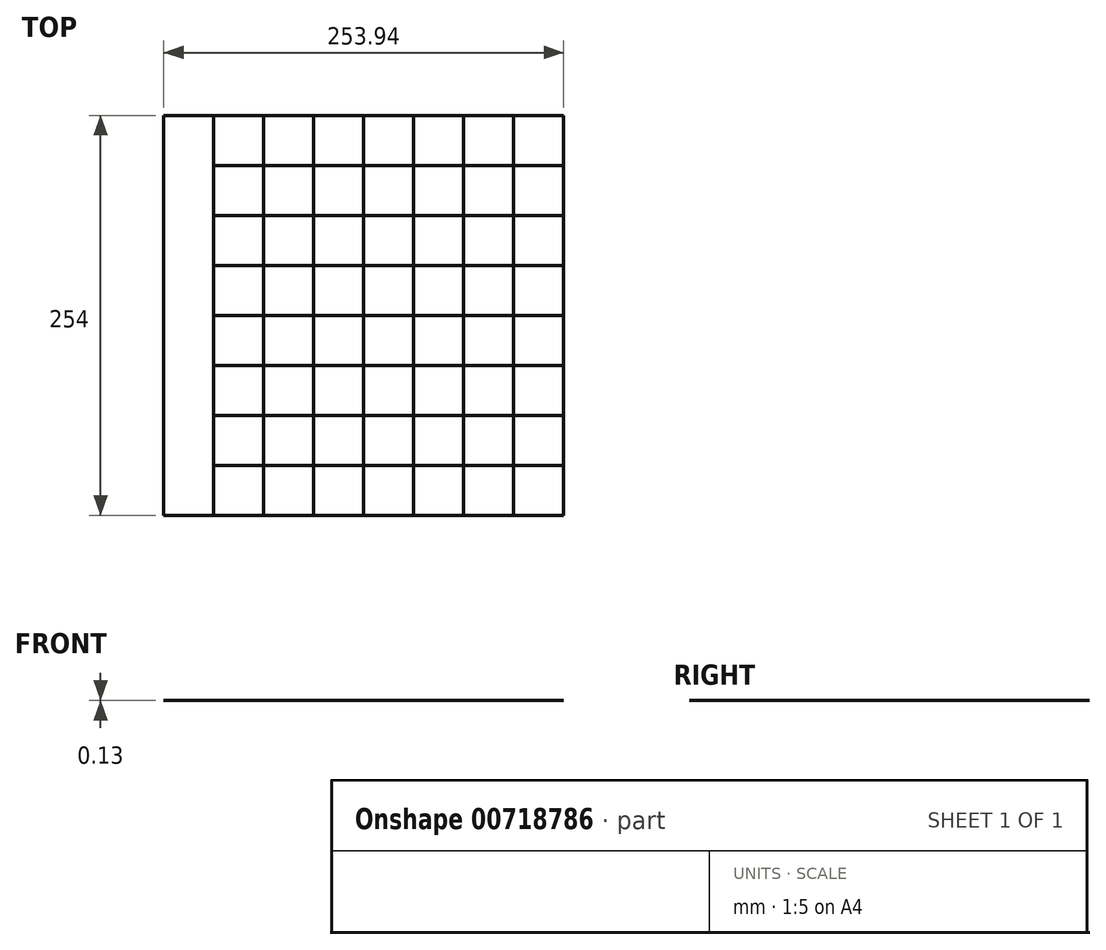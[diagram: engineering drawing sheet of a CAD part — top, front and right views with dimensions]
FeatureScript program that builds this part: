
annotation { "Feature Type Name" : "Feature", "Feature Type Description" : "" }
export const myFeature = defineFeature(function(context is Context, id is Id, definition is map)
    precondition{}
    {
        {
            var Q0;
            Q0=qCreatedBy(makeId("Top.planeOp"),FACE);
            var sketch = newSketch(context, id + "F0", { "sketchPlane" : qUnion([Q0])});
            skLineSegment(sketch, "E0.bottom", {"start": v(-104.6, 172.24) * mm, "end": v(149.4, 172.24) * mm});
            skLineSegment(sketch, "E0.top", {"start": v(-104.6, -81.76) * mm, "end": v(149.4, -81.76) * mm});
            skLineSegment(sketch, "E0.left", {"start": v(-104.6, 172.24) * mm, "end": v(-104.6, -81.76) * mm});
            skLineSegment(sketch, "E0.right", {"start": v(149.4, 172.24) * mm, "end": v(149.4, -81.76) * mm});
            skLineSegment(sketch, "E1", {"start": v(22.4, 172.24) * mm, "end": v(22.4, -81.76) * mm});
            skLineSegment(sketch, "E2", {"start": v(-41.1, 172.24) * mm, "end": v(-41.1, -81.76) * mm});
            skLineSegment(sketch, "E3", {"start": v(-72.86, 172.24) * mm, "end": v(-72.86, -81.76) * mm});
            skLineSegment(sketch, "E4", {"start": v(-9.36, 172.24) * mm, "end": v(-9.36, -81.76) * mm});
            skLineSegment(sketch, "E5", {"start": v(85.9, 172.24) * mm, "end": v(85.9, -81.76) * mm});
            skLineSegment(sketch, "E6", {"start": v(54.14, 172.24) * mm, "end": v(54.14, -81.76) * mm});
            skLineSegment(sketch, "E7", {"start": v(117.64, 172.24) * mm, "end": v(117.64, -81.76) * mm});
            skLineSegment(sketch, "E8.bottom", {"start": v(-104.55, -81.76) * mm, "end": v(-104.55, 172.24) * mm});
            skLineSegment(sketch, "E8.top", {"start": v(-72.8, -81.76) * mm, "end": v(-72.8, 172.24) * mm});
            skLineSegment(sketch, "E8.left", {"start": v(-104.55, -81.76) * mm, "end": v(-72.8, -81.76) * mm});
            skLineSegment(sketch, "E8.right", {"start": v(-104.55, 172.24) * mm, "end": v(-72.8, 172.24) * mm});
            skLineSegment(sketch, "E9", {"start": v(-104.55, 140.5) * mm, "end": v(149.4, 140.5) * mm});
            skLineSegment(sketch, "E10", {"start": v(-104.55, 108.74) * mm, "end": v(149.4, 108.74) * mm});
            skLineSegment(sketch, "E11", {"start": v(-104.55, 77) * mm, "end": v(149.4, 77) * mm});
            skLineSegment(sketch, "E12", {"start": v(-104.55, 45.24) * mm, "end": v(149.4, 45.24) * mm});
            skLineSegment(sketch, "E13", {"start": v(-104.55, 13.5) * mm, "end": v(149.4, 13.5) * mm});
            skLineSegment(sketch, "E14", {"start": v(-104.55, -18.26) * mm, "end": v(149.4, -18.26) * mm});
            skLineSegment(sketch, "E15", {"start": v(-104.55, -50) * mm, "end": v(149.4, -50) * mm});
            skSolve(sketch);
        }
        {
            var Q0;
            {var subQ0=sQuery(id+"F0.wireOp",EDGE,"E8.right");var subQ1=sQuery(id+"F0.wireOp",EDGE,"E3");var subQ2=makeQuery(id+"F0.imprint","INTERSECT",VERTEX,{"derivedFrom":[subQ1,subQ0]});Q0=makeQuery(id+"F0.imprint","IMPRINT",FACE,{"disambiguationData":[TD([[makeQuery(id+"F0.imprint","IMPRINT",EDGE,{"disambiguationData":[TD([[subQ2,-1.0]])],"derivedFrom":subQ1}),-1.0]])]});}
            var Q1;
            {var subQ0=sQuery(id+"F0.wireOp",EDGE,"E9");var subQ1=sQuery(id+"F0.wireOp",EDGE,"E2");var subQ2=makeQuery(id+"F0.imprint","INTERSECT",VERTEX,{"derivedFrom":[subQ1,subQ0]});Q1=makeQuery(id+"F0.imprint","IMPRINT",FACE,{"disambiguationData":[TD([[makeQuery(id+"F0.imprint","IMPRINT",EDGE,{"disambiguationData":[TD([[subQ2,-1.0]])],"derivedFrom":subQ1}),-1.0]])]});}
            var Q2;
            {var subQ0=sQuery(id+"F0.wireOp",EDGE,"E2");var subQ1=sQuery(id+"F0.wireOp",EDGE,"E0.bottom");var subQ2=makeQuery(id+"F0.imprint","INTERSECT",VERTEX,{"derivedFrom":[subQ1,subQ0]});Q2=makeQuery(id+"F0.imprint","IMPRINT",FACE,{"disambiguationData":[TD([[makeQuery(id+"F0.imprint","IMPRINT",EDGE,{"disambiguationData":[TD([[subQ2,-1.0]])],"derivedFrom":subQ1}),-1.0]])]});}
            var Q3;
            {var subQ0=sQuery(id+"F0.wireOp",EDGE,"E9");var subQ1=sQuery(id+"F0.wireOp",EDGE,"E1");var subQ2=makeQuery(id+"F0.imprint","INTERSECT",VERTEX,{"derivedFrom":[subQ1,subQ0]});Q3=makeQuery(id+"F0.imprint","IMPRINT",FACE,{"disambiguationData":[TD([[makeQuery(id+"F0.imprint","IMPRINT",EDGE,{"disambiguationData":[TD([[subQ2,-1.0]])],"derivedFrom":subQ1}),-1.0]])]});}
            var Q4;
            {var subQ0=sQuery(id+"F0.wireOp",EDGE,"E1");var subQ1=sQuery(id+"F0.wireOp",EDGE,"E0.bottom");var subQ2=makeQuery(id+"F0.imprint","INTERSECT",VERTEX,{"derivedFrom":[subQ1,subQ0]});Q4=makeQuery(id+"F0.imprint","IMPRINT",FACE,{"disambiguationData":[TD([[makeQuery(id+"F0.imprint","IMPRINT",EDGE,{"disambiguationData":[TD([[subQ2,-1.0]])],"derivedFrom":subQ1}),-1.0]])]});}
            var Q5;
            {var subQ0=sQuery(id+"F0.wireOp",EDGE,"E9");var subQ1=sQuery(id+"F0.wireOp",EDGE,"E5");var subQ2=makeQuery(id+"F0.imprint","INTERSECT",VERTEX,{"derivedFrom":[subQ1,subQ0]});Q5=makeQuery(id+"F0.imprint","IMPRINT",FACE,{"disambiguationData":[TD([[makeQuery(id+"F0.imprint","IMPRINT",EDGE,{"disambiguationData":[TD([[subQ2,-1.0]])],"derivedFrom":subQ1}),-1.0]])]});}
            var Q6;
            {var subQ0=sQuery(id+"F0.wireOp",EDGE,"E5");var subQ1=sQuery(id+"F0.wireOp",EDGE,"E0.bottom");var subQ2=makeQuery(id+"F0.imprint","INTERSECT",VERTEX,{"derivedFrom":[subQ1,subQ0]});Q6=makeQuery(id+"F0.imprint","IMPRINT",FACE,{"disambiguationData":[TD([[makeQuery(id+"F0.imprint","IMPRINT",EDGE,{"disambiguationData":[TD([[subQ2,-1.0]])],"derivedFrom":subQ1}),-1.0]])]});}
            var Q7;
            {var subQ0=sQuery(id+"F0.wireOp",EDGE,"E9");var subQ1=sQuery(id+"F0.wireOp",EDGE,"E0.right");var subQ2=makeQuery(id+"F0.imprint","INTERSECT",VERTEX,{"derivedFrom":[subQ1,subQ0]});Q7=makeQuery(id+"F0.imprint","IMPRINT",FACE,{"disambiguationData":[TD([[makeQuery(id+"F0.imprint","IMPRINT",EDGE,{"disambiguationData":[TD([[subQ2,-1.0]])],"derivedFrom":subQ1}),-1.0]])]});}
            var Q8;
            {var subQ0=sQuery(id+"F0.wireOp",EDGE,"E10");var subQ1=sQuery(id+"F0.wireOp",EDGE,"E5");var subQ2=makeQuery(id+"F0.imprint","INTERSECT",VERTEX,{"derivedFrom":[subQ1,subQ0]});Q8=makeQuery(id+"F0.imprint","IMPRINT",FACE,{"disambiguationData":[TD([[makeQuery(id+"F0.imprint","IMPRINT",EDGE,{"disambiguationData":[TD([[subQ2,-1.0]])],"derivedFrom":subQ1}),1.0]])]});}
            var Q9;
            {var subQ0=sQuery(id+"F0.wireOp",EDGE,"E11");var subQ1=sQuery(id+"F0.wireOp",EDGE,"E5");var subQ2=makeQuery(id+"F0.imprint","INTERSECT",VERTEX,{"derivedFrom":[subQ1,subQ0]});Q9=makeQuery(id+"F0.imprint","IMPRINT",FACE,{"disambiguationData":[TD([[makeQuery(id+"F0.imprint","IMPRINT",EDGE,{"disambiguationData":[TD([[subQ2,-1.0]])],"derivedFrom":subQ1}),-1.0]])]});}
            var Q10;
            {var subQ0=sQuery(id+"F0.wireOp",EDGE,"E10");var subQ1=sQuery(id+"F0.wireOp",EDGE,"E1");var subQ2=makeQuery(id+"F0.imprint","INTERSECT",VERTEX,{"derivedFrom":[subQ1,subQ0]});Q10=makeQuery(id+"F0.imprint","IMPRINT",FACE,{"disambiguationData":[TD([[makeQuery(id+"F0.imprint","IMPRINT",EDGE,{"disambiguationData":[TD([[subQ2,-1.0]])],"derivedFrom":subQ1}),1.0]])]});}
            var Q11;
            {var subQ0=sQuery(id+"F0.wireOp",EDGE,"E11");var subQ1=sQuery(id+"F0.wireOp",EDGE,"E1");var subQ2=makeQuery(id+"F0.imprint","INTERSECT",VERTEX,{"derivedFrom":[subQ1,subQ0]});Q11=makeQuery(id+"F0.imprint","IMPRINT",FACE,{"disambiguationData":[TD([[makeQuery(id+"F0.imprint","IMPRINT",EDGE,{"disambiguationData":[TD([[subQ2,-1.0]])],"derivedFrom":subQ1}),-1.0]])]});}
            var Q12;
            {var subQ0=sQuery(id+"F0.wireOp",EDGE,"E10");var subQ1=sQuery(id+"F0.wireOp",EDGE,"E2");var subQ2=makeQuery(id+"F0.imprint","INTERSECT",VERTEX,{"derivedFrom":[subQ1,subQ0]});Q12=makeQuery(id+"F0.imprint","IMPRINT",FACE,{"disambiguationData":[TD([[makeQuery(id+"F0.imprint","IMPRINT",EDGE,{"disambiguationData":[TD([[subQ2,-1.0]])],"derivedFrom":subQ1}),1.0]])]});}
            var Q13;
            {var subQ0=sQuery(id+"F0.wireOp",EDGE,"E11");var subQ1=sQuery(id+"F0.wireOp",EDGE,"E2");var subQ2=makeQuery(id+"F0.imprint","INTERSECT",VERTEX,{"derivedFrom":[subQ1,subQ0]});Q13=makeQuery(id+"F0.imprint","IMPRINT",FACE,{"disambiguationData":[TD([[makeQuery(id+"F0.imprint","IMPRINT",EDGE,{"disambiguationData":[TD([[subQ2,-1.0]])],"derivedFrom":subQ1}),-1.0]])]});}
            var Q14;
            {var subQ0=sQuery(id+"F0.wireOp",EDGE,"E10");var subQ1=sQuery(id+"F0.wireOp",EDGE,"E3");var subQ2=makeQuery(id+"F0.imprint","INTERSECT",VERTEX,{"derivedFrom":[subQ1,subQ0]});Q14=makeQuery(id+"F0.imprint","IMPRINT",FACE,{"disambiguationData":[TD([[makeQuery(id+"F0.imprint","IMPRINT",EDGE,{"disambiguationData":[TD([[subQ2,-1.0]])],"derivedFrom":subQ1}),-1.0]])]});}
            var Q15;
            {var subQ0=sQuery(id+"F0.wireOp",EDGE,"E12");var subQ1=sQuery(id+"F0.wireOp",EDGE,"E3");var subQ2=makeQuery(id+"F0.imprint","INTERSECT",VERTEX,{"derivedFrom":[subQ1,subQ0]});Q15=makeQuery(id+"F0.imprint","IMPRINT",FACE,{"disambiguationData":[TD([[makeQuery(id+"F0.imprint","IMPRINT",EDGE,{"disambiguationData":[TD([[subQ2,-1.0]])],"derivedFrom":subQ1}),-1.0]])]});}
            var Q16;
            {var subQ0=sQuery(id+"F0.wireOp",EDGE,"E13");var subQ1=sQuery(id+"F0.wireOp",EDGE,"E2");var subQ2=makeQuery(id+"F0.imprint","INTERSECT",VERTEX,{"derivedFrom":[subQ1,subQ0]});Q16=makeQuery(id+"F0.imprint","IMPRINT",FACE,{"disambiguationData":[TD([[makeQuery(id+"F0.imprint","IMPRINT",EDGE,{"disambiguationData":[TD([[subQ2,-1.0]])],"derivedFrom":subQ1}),-1.0]])]});}
            var Q17;
            {var subQ0=sQuery(id+"F0.wireOp",EDGE,"E12");var subQ1=sQuery(id+"F0.wireOp",EDGE,"E2");var subQ2=makeQuery(id+"F0.imprint","INTERSECT",VERTEX,{"derivedFrom":[subQ1,subQ0]});Q17=makeQuery(id+"F0.imprint","IMPRINT",FACE,{"disambiguationData":[TD([[makeQuery(id+"F0.imprint","IMPRINT",EDGE,{"disambiguationData":[TD([[subQ2,-1.0]])],"derivedFrom":subQ1}),1.0]])]});}
            var Q18;
            {var subQ0=sQuery(id+"F0.wireOp",EDGE,"E13");var subQ1=sQuery(id+"F0.wireOp",EDGE,"E1");var subQ2=makeQuery(id+"F0.imprint","INTERSECT",VERTEX,{"derivedFrom":[subQ1,subQ0]});Q18=makeQuery(id+"F0.imprint","IMPRINT",FACE,{"disambiguationData":[TD([[makeQuery(id+"F0.imprint","IMPRINT",EDGE,{"disambiguationData":[TD([[subQ2,-1.0]])],"derivedFrom":subQ1}),-1.0]])]});}
            var Q19;
            {var subQ0=sQuery(id+"F0.wireOp",EDGE,"E12");var subQ1=sQuery(id+"F0.wireOp",EDGE,"E1");var subQ2=makeQuery(id+"F0.imprint","INTERSECT",VERTEX,{"derivedFrom":[subQ1,subQ0]});Q19=makeQuery(id+"F0.imprint","IMPRINT",FACE,{"disambiguationData":[TD([[makeQuery(id+"F0.imprint","IMPRINT",EDGE,{"disambiguationData":[TD([[subQ2,-1.0]])],"derivedFrom":subQ1}),1.0]])]});}
            var Q20;
            {var subQ0=sQuery(id+"F0.wireOp",EDGE,"E13");var subQ1=sQuery(id+"F0.wireOp",EDGE,"E5");var subQ2=makeQuery(id+"F0.imprint","INTERSECT",VERTEX,{"derivedFrom":[subQ1,subQ0]});Q20=makeQuery(id+"F0.imprint","IMPRINT",FACE,{"disambiguationData":[TD([[makeQuery(id+"F0.imprint","IMPRINT",EDGE,{"disambiguationData":[TD([[subQ2,-1.0]])],"derivedFrom":subQ1}),-1.0]])]});}
            var Q21;
            {var subQ0=sQuery(id+"F0.wireOp",EDGE,"E12");var subQ1=sQuery(id+"F0.wireOp",EDGE,"E5");var subQ2=makeQuery(id+"F0.imprint","INTERSECT",VERTEX,{"derivedFrom":[subQ1,subQ0]});Q21=makeQuery(id+"F0.imprint","IMPRINT",FACE,{"disambiguationData":[TD([[makeQuery(id+"F0.imprint","IMPRINT",EDGE,{"disambiguationData":[TD([[subQ2,-1.0]])],"derivedFrom":subQ1}),1.0]])]});}
            var Q22;
            {var subQ0=sQuery(id+"F0.wireOp",EDGE,"E13");var subQ1=sQuery(id+"F0.wireOp",EDGE,"E0.right");var subQ2=makeQuery(id+"F0.imprint","INTERSECT",VERTEX,{"derivedFrom":[subQ1,subQ0]});Q22=makeQuery(id+"F0.imprint","IMPRINT",FACE,{"disambiguationData":[TD([[makeQuery(id+"F0.imprint","IMPRINT",EDGE,{"disambiguationData":[TD([[subQ2,-1.0]])],"derivedFrom":subQ1}),-1.0]])]});}
            var Q23;
            {var subQ0=sQuery(id+"F0.wireOp",EDGE,"E11");var subQ1=sQuery(id+"F0.wireOp",EDGE,"E0.right");var subQ2=makeQuery(id+"F0.imprint","INTERSECT",VERTEX,{"derivedFrom":[subQ1,subQ0]});Q23=makeQuery(id+"F0.imprint","IMPRINT",FACE,{"disambiguationData":[TD([[makeQuery(id+"F0.imprint","IMPRINT",EDGE,{"disambiguationData":[TD([[subQ2,-1.0]])],"derivedFrom":subQ1}),-1.0]])]});}
            var Q24;
            {var subQ0=sQuery(id+"F0.wireOp",EDGE,"E14");var subQ1=sQuery(id+"F0.wireOp",EDGE,"E3");var subQ2=makeQuery(id+"F0.imprint","INTERSECT",VERTEX,{"derivedFrom":[subQ1,subQ0]});Q24=makeQuery(id+"F0.imprint","IMPRINT",FACE,{"disambiguationData":[TD([[makeQuery(id+"F0.imprint","IMPRINT",EDGE,{"disambiguationData":[TD([[subQ2,-1.0]])],"derivedFrom":subQ1}),-1.0]])]});}
            var Q25;
            {var subQ0=sQuery(id+"F0.wireOp",EDGE,"E2");var subQ1=sQuery(id+"F0.wireOp",EDGE,"E0.top");var subQ2=makeQuery(id+"F0.imprint","INTERSECT",VERTEX,{"derivedFrom":[subQ1,subQ0]});Q25=makeQuery(id+"F0.imprint","IMPRINT",FACE,{"disambiguationData":[TD([[makeQuery(id+"F0.imprint","IMPRINT",EDGE,{"disambiguationData":[TD([[subQ2,1.0]])],"derivedFrom":subQ0}),-1.0]])]});}
            var Q26;
            {var subQ0=sQuery(id+"F0.wireOp",EDGE,"E14");var subQ1=sQuery(id+"F0.wireOp",EDGE,"E2");var subQ2=makeQuery(id+"F0.imprint","INTERSECT",VERTEX,{"derivedFrom":[subQ1,subQ0]});Q26=makeQuery(id+"F0.imprint","IMPRINT",FACE,{"disambiguationData":[TD([[makeQuery(id+"F0.imprint","IMPRINT",EDGE,{"disambiguationData":[TD([[subQ2,-1.0]])],"derivedFrom":subQ1}),1.0]])]});}
            var Q27;
            {var subQ0=sQuery(id+"F0.wireOp",EDGE,"E1");var subQ1=sQuery(id+"F0.wireOp",EDGE,"E0.top");var subQ2=makeQuery(id+"F0.imprint","INTERSECT",VERTEX,{"derivedFrom":[subQ1,subQ0]});Q27=makeQuery(id+"F0.imprint","IMPRINT",FACE,{"disambiguationData":[TD([[makeQuery(id+"F0.imprint","IMPRINT",EDGE,{"disambiguationData":[TD([[subQ2,1.0]])],"derivedFrom":subQ1}),1.0]])]});}
            var Q28;
            {var subQ0=sQuery(id+"F0.wireOp",EDGE,"E5");var subQ1=sQuery(id+"F0.wireOp",EDGE,"E0.top");var subQ2=makeQuery(id+"F0.imprint","INTERSECT",VERTEX,{"derivedFrom":[subQ1,subQ0]});Q28=makeQuery(id+"F0.imprint","IMPRINT",FACE,{"disambiguationData":[TD([[makeQuery(id+"F0.imprint","IMPRINT",EDGE,{"disambiguationData":[TD([[subQ2,1.0]])],"derivedFrom":subQ1}),1.0]])]});}
            var Q29;
            {var subQ0=sQuery(id+"F0.wireOp",EDGE,"E0.right");var subQ1=sQuery(id+"F0.wireOp",EDGE,"E0.top");var subQ2=makeQuery(id+"F0.imprint","INTERSECT",VERTEX,{"derivedFrom":[subQ1,subQ0]});Q29=makeQuery(id+"F0.imprint","IMPRINT",FACE,{"disambiguationData":[TD([[makeQuery(id+"F0.imprint","IMPRINT",EDGE,{"disambiguationData":[TD([[subQ2,1.0]])],"derivedFrom":subQ1}),1.0]])]});}
            var Q30;
            {var subQ0=sQuery(id+"F0.wireOp",EDGE,"E14");var subQ1=sQuery(id+"F0.wireOp",EDGE,"E1");var subQ2=makeQuery(id+"F0.imprint","INTERSECT",VERTEX,{"derivedFrom":[subQ1,subQ0]});Q30=makeQuery(id+"F0.imprint","IMPRINT",FACE,{"disambiguationData":[TD([[makeQuery(id+"F0.imprint","IMPRINT",EDGE,{"disambiguationData":[TD([[subQ2,-1.0]])],"derivedFrom":subQ1}),1.0]])]});}
            var Q31;
            {var subQ0=sQuery(id+"F0.wireOp",EDGE,"E14");var subQ1=sQuery(id+"F0.wireOp",EDGE,"E5");var subQ2=makeQuery(id+"F0.imprint","INTERSECT",VERTEX,{"derivedFrom":[subQ1,subQ0]});Q31=makeQuery(id+"F0.imprint","IMPRINT",FACE,{"disambiguationData":[TD([[makeQuery(id+"F0.imprint","IMPRINT",EDGE,{"disambiguationData":[TD([[subQ2,-1.0]])],"derivedFrom":subQ1}),1.0]])]});}
            extrude(context, id + "F1", {"entities" : qUnion([Q0, Q1, Q2, Q3, Q4, Q5, Q6, Q7, Q8, Q9, Q10, Q11, Q12, Q13, Q14, Q15, Q16, Q17, Q18, Q19, Q20, Q21, Q22, Q23, Q24, Q25, Q26, Q27, Q28, Q29, Q30, Q31]), "depth" : 0.13 * mm, "offsetDistance" : 25.4 * mm});
        }
        {
            var Q0;
            Q0=qCreatedBy(makeId("Top.planeOp"),FACE);
            var sketch = newSketch(context, id + "F2", { "sketchPlane" : qUnion([Q0])});
            skLineSegment(sketch, "E16.bottom", {"start": v(22.4, 172.24) * mm, "end": v(149.4, 172.24) * mm});
            skLineSegment(sketch, "E16.top", {"start": v(22.4, -81.76) * mm, "end": v(149.4, -81.76) * mm});
            skLineSegment(sketch, "E16.left", {"start": v(22.4, 172.24) * mm, "end": v(22.4, -81.76) * mm});
            skLineSegment(sketch, "E16.right", {"start": v(149.4, 172.24) * mm, "end": v(149.4, -81.76) * mm});
            skSolve(sketch);
        }
        {
            var Q0;
            Q0 = qSketchRegion(id + "F2", true);
            extrude(context, id + "F3", {"entities" : qUnion([Q0]), "oppositeDirection" : true, "depth" : 0 * mm, "offsetDistance" : 25.4 * mm});
        }
        {
            var Q0;
            Q0=qCreatedBy(makeId("Top.planeOp"),FACE);
            var sketch = newSketch(context, id + "F4", { "sketchPlane" : qUnion([Q0])});
            skLineSegment(sketch, "E17.bottom", {"start": v(-104.55, 172.24) * mm, "end": v(22.45, 172.24) * mm});
            skLineSegment(sketch, "E17.top", {"start": v(-104.55, -81.76) * mm, "end": v(22.45, -81.76) * mm});
            skLineSegment(sketch, "E17.left", {"start": v(-104.55, 172.24) * mm, "end": v(-104.55, -81.76) * mm});
            skLineSegment(sketch, "E17.right", {"start": v(22.45, 172.24) * mm, "end": v(22.45, -81.76) * mm});
            skSolve(sketch);
        }
        {
            var Q0;
            Q0 = qSketchRegion(id + "F4", true);
            extrude(context, id + "F5", {"entities" : qUnion([Q0]), "oppositeDirection" : true, "depth" : 0 * mm, "offsetDistance" : 25.4 * mm});
        }
    });
